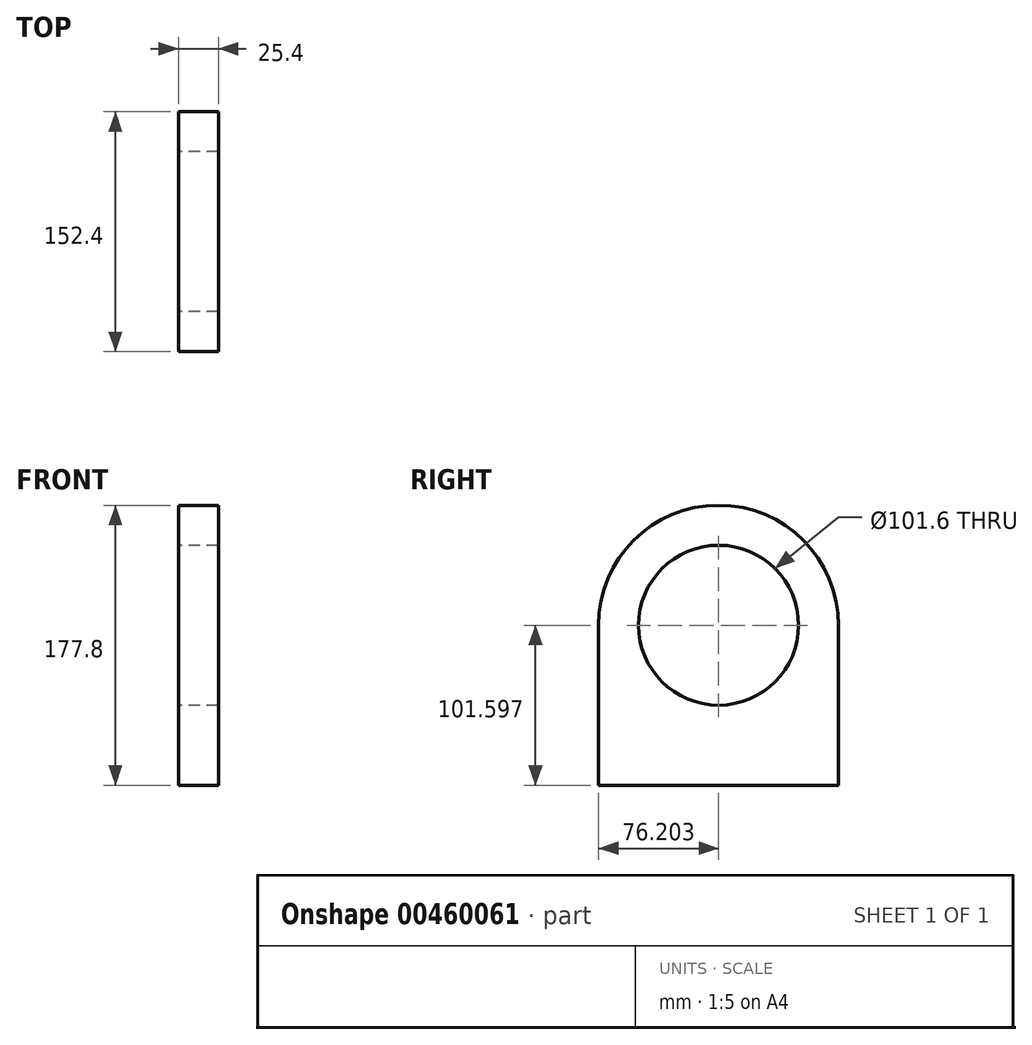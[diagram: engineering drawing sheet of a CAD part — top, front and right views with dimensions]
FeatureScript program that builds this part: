
annotation { "Feature Type Name" : "Feature", "Feature Type Description" : "" }
export const myFeature = defineFeature(function(context is Context, id is Id, definition is map)
    precondition{}
    {
        {
            var Q0;
            Q0=qCreatedBy(makeId("Right.planeOp"),FACE);
            var sketch = newSketch(context, id + "F0", { "sketchPlane" : qUnion([Q0])});
            skLineSegment(sketch, "E0.bottom", {"start": v(-142.4, -279.9) * mm, "end": v(10, -279.9) * mm});
            skLineSegment(sketch, "E0.top", {"start": v(-142.4, -178.3) * mm, "end": v(10, -178.3) * mm});
            skLineSegment(sketch, "E0.left", {"start": v(-142.4, -279.9) * mm, "end": v(-142.4, -178.3) * mm});
            skLineSegment(sketch, "E0.right", {"start": v(10, -279.9) * mm, "end": v(10, -178.3) * mm});
            skCircle(sketch, "E1", {"center": v(-66.2, -178.3) * mm, "radius": 76.2 * mm});
            skCircle(sketch, "E2", {"center": v(-66.2, -178.3) * mm, "radius": 50.8 * mm});
            skSolve(sketch);
        }
        {
            var Q0;
            Q0 = qSketchRegion(id + "F0", true);
            extrude(context, id + "F1", {"entities" : qUnion([Q0]), "depth" : 25.4 * mm});
        }
    });
